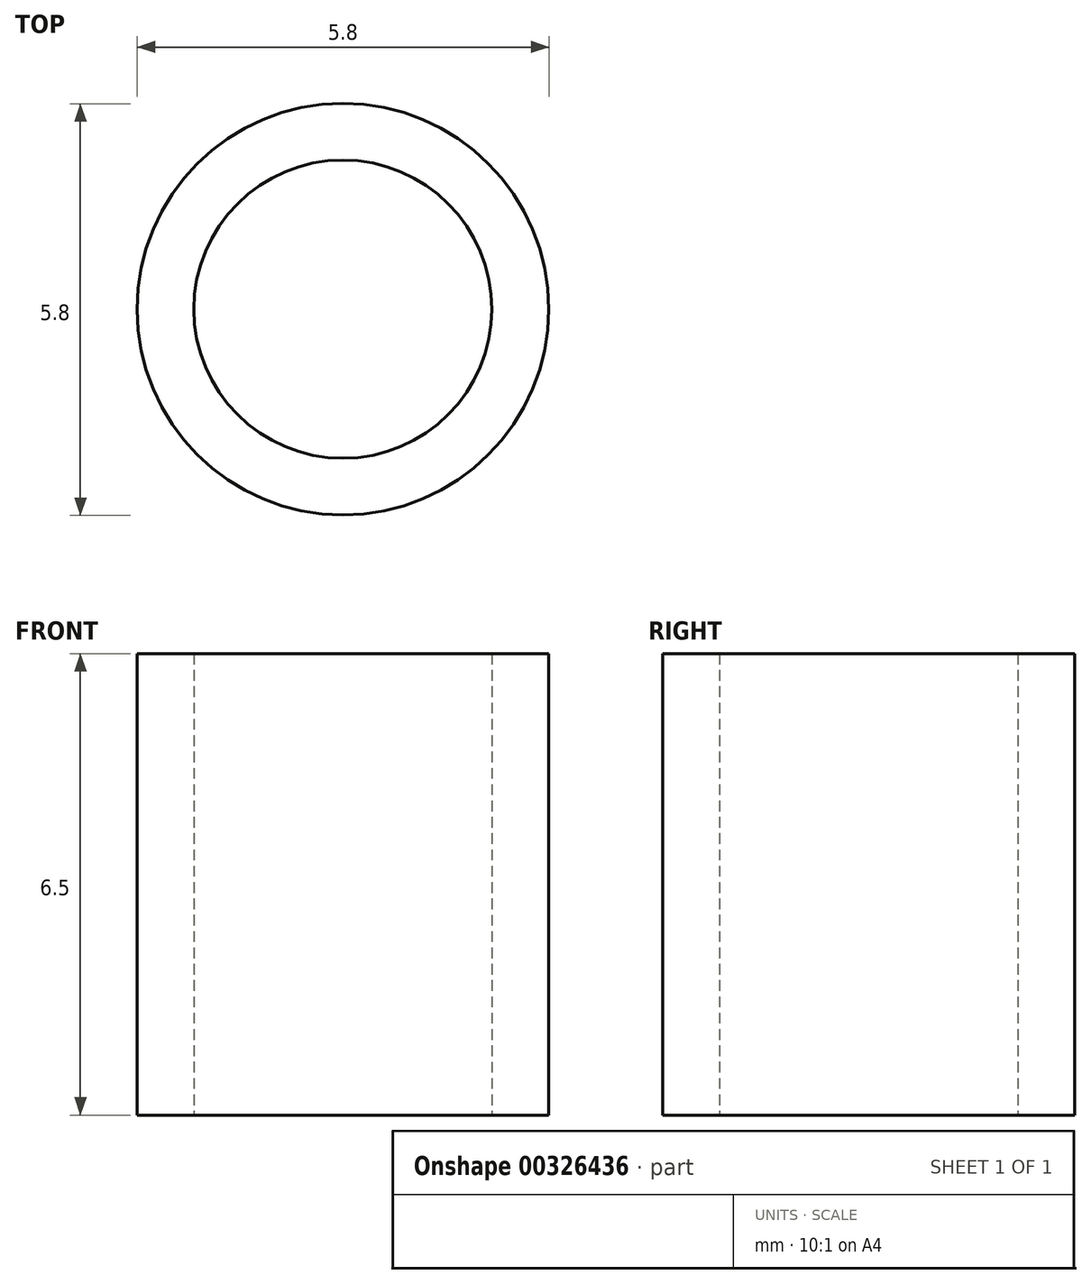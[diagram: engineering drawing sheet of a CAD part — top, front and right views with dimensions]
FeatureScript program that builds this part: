
annotation { "Feature Type Name" : "Feature", "Feature Type Description" : "" }
export const myFeature = defineFeature(function(context is Context, id is Id, definition is map)
    precondition{}
    {
        {
            var Q0;
            Q0=qCreatedBy(makeId("Top.planeOp"),FACE);
            var sketch = newSketch(context, id + "F0", { "sketchPlane" : qUnion([Q0])});
            skCircle(sketch, "E0", {"center": v(-32.1, 26.84) * mm, "radius": 2.9 * mm});
            skCircle(sketch, "E1", {"center": v(-32.1, 26.84) * mm, "radius": 2.1 * mm});
            skSolve(sketch);
        }
        {
            var Q0;
            Q0=makeQuery(id+"F0.imprint","IMPRINT",FACE,{"disambiguationData":[TD([[makeQuery(id+"F0.imprint","IMPRINT",EDGE,{"derivedFrom":sQuery(id+"F0.wireOp",EDGE,"E0")}),1.0]])]});
            var Q1;
            Q1=sQuery(id+"F0.wireOp",EDGE,"E1");
            var Q2;
            Q2=sQuery(id+"F0.wireOp",EDGE,"E0");
            extrude(context, id + "F1", {"entities" : qUnion([Q0]), "surfaceEntities" : qUnion([Q1, Q2]), "depth" : 6.5 * mm});
        }
    });
